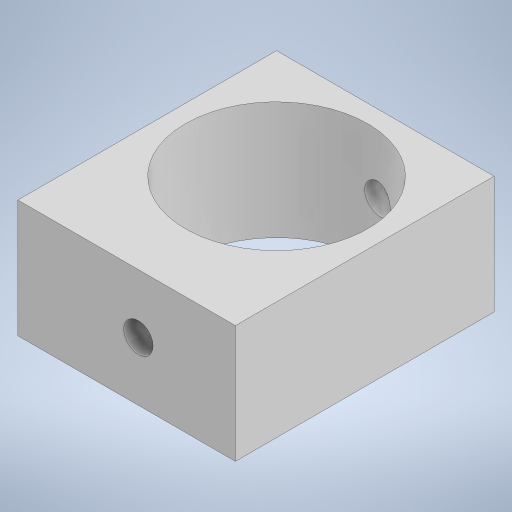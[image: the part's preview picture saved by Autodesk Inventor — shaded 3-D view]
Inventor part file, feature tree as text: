
AUTODESK INVENTOR PART (.ipt)
format: ipt  version: 2023 (Build 270158000, 158)  size: 237,056 bytes
history: native  units: in
note: dims shown in document units (in); Inventor stores cm internally (conversion verified against a paired STEP export)
features: extrude x5, sketch x5
ambient origin geometry x8: Origin, YZ Plane, XZ Plane, XY Plane, X Axis, Y Axis, Z Axis, Center Point
bodies: Solid1 (feature_tree)
feature tree (10):
  extrude  "Extrusion1"  Depth=1.4567in
  extrude  "Extrusion2"  Depth=0.7283in
  extrude  "Extrusion3"  Depth=0.7874in TaperAngle=0.0deg
  extrude  "Extrusion4"  Depth=0.1969in TaperAngle=0.0deg
  extrude  "Extrusion5"  Depth=0.1969in TaperAngle=0.0deg
  sketch  "Sketch1"  dims[d0=1.4567in d1=1.4567in]
  sketch  "Sketch3"  dims[d2=0.7283in d3=0.7283in]
  sketch  "Sketch4"  dims[d4=1.2205in d5=0.7874in d6=0.0in]
  sketch  "Sketch5"  dims[d8=0.3543in d9=0.1969in d10=0.0in]
  sketch  "Sketch6"  dims[d11=0.1969in d12=0.1969in d13=0.0in d14=0.0787in d15=0.0in d16=0.1969in d17=0.0in]
